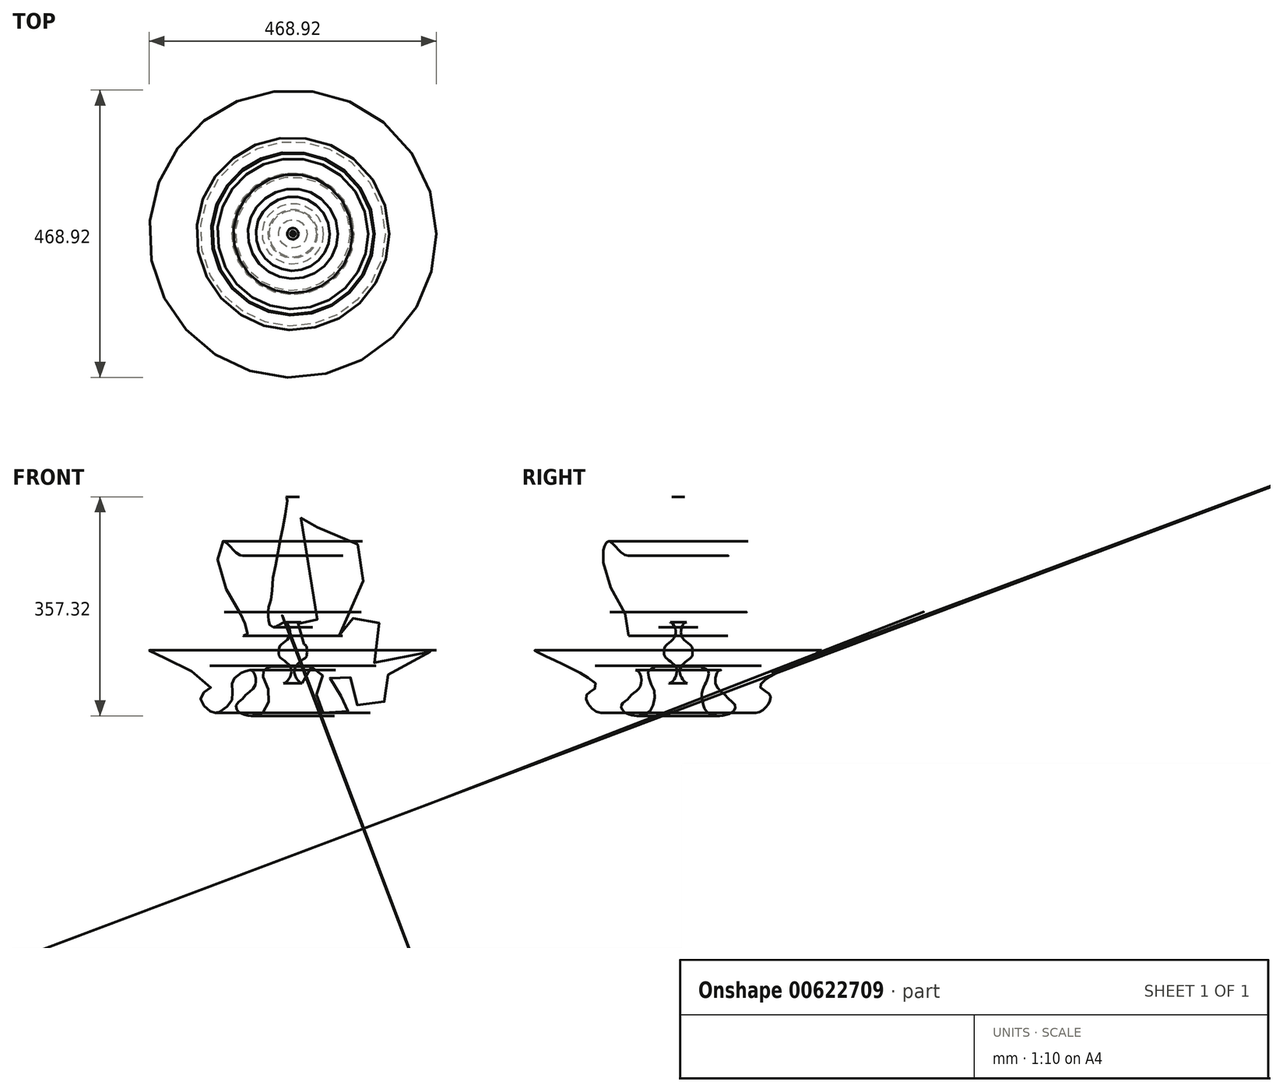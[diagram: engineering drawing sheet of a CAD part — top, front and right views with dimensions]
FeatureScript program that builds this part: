
annotation { "Feature Type Name" : "Feature", "Feature Type Description" : "" }
export const myFeature = defineFeature(function(context is Context, id is Id, definition is map)
    precondition{}
    {
        {
            var Q0;
            Q0=qCreatedBy(makeId("Top.planeOp"),FACE);
            var sketch = newSketch(context, id + "F0", { "sketchPlane" : qUnion([Q0])});
            skCircle(sketch, "E0", {"center": v(0, 0) * mm, "radius": 40 * mm});
            skSolve(sketch);
        }
        {
            var Q0;
            Q0=qCreatedBy(makeId("Front.planeOp"),FACE);
            var sketch = newSketch(context, id + "F1", { "sketchPlane" : qUnion([Q0])});
            skFitSpline(sketch, "E1", {"points": [v(18.5, 10.16) * mm, v(6.63, 20.9) * mm, v(5.5, 37.26) * mm, v(12.84, 46.02) * mm, v(26.4, 39.52) * mm, v(39.1, 45.45) * mm, v(10.22, 250.55) * mm, v(77.92, 155.1) * mm, v(112.22, 178.01) * mm, v(118.87, 125.7) * mm, v(74.67, 25.69) * mm, v(98.1, 30.77) * mm, v(96.97, 47.7) * mm, v(108.26, 61.82) * mm, v(125.48, 56.18) * mm, v(156.45, 11.08) * mm, v(132.67, -24.59) * mm, v(234.44, 0) * mm, v(133.62, -56.45) * mm, v(149.76, -72.83) * mm, v(131.98, -100.5) * mm, v(109.96, -93.73) * mm, v(98.1, -75.66) * mm, v(98.67, -51.1) * mm, v(75.23, -33.03) * mm, v(64.5, -34.44) * mm, v(60.84, -53.92) * mm, v(67.9, -65.78) * mm, v(75.8, -71.99) * mm, v(84.55, -81.3) * mm, v(92.17, -87.8) * mm, v(91.9, -95.98) * mm, v(85.4, -102.2) * mm, v(66.77, -106.71) * mm, v(46.44, -99.94) * mm, v(42.2, -92.03) * mm, v(38.82, -80.46) * mm, v(38.82, -68.88) * mm, v(41.64, -60.13) * mm, v(47.29, -47.7) * mm, v(48.98, -39.24) * mm, v(49.54, -36.42) * mm, v(49.54, -35.57) * mm, v(42.77, -29.08) * mm, v(29.22, -27.1) * mm, v(23.3, -36.14) * mm, v(21.88, -40.65) * mm, v(15.95, -53.64) * mm, v(3.25, -39.8) * mm, v(5.79, -24.56) * mm, v(17.93, -13.83) * mm, v(22.44, -9.03) * mm, v(23, 0) * mm, v(22.16, 5.65) * mm, v(18.5, 10.16) * mm]});
            skSolve(sketch);
        }
        {
            var Q0;
            Q0=makeQuery(id+"F1.imprint","IMPRINT",FACE,{"disambiguationData":[TD([[makeQuery(id+"F1.imprint","IMPRINT",EDGE,{"derivedFrom":sQuery(id+"F1.wireOp",EDGE,"E1")}),-1.0]])]});
            var Q1;
            Q1=sQuery(id+"F0.wireOp",EDGE,"E0");
            revolve(context, id + "F2", {"entities" : qUnion([Q0]), "axis" : qUnion([Q1]), "revolveType" : RevolveType.FULL});
        }
    });
